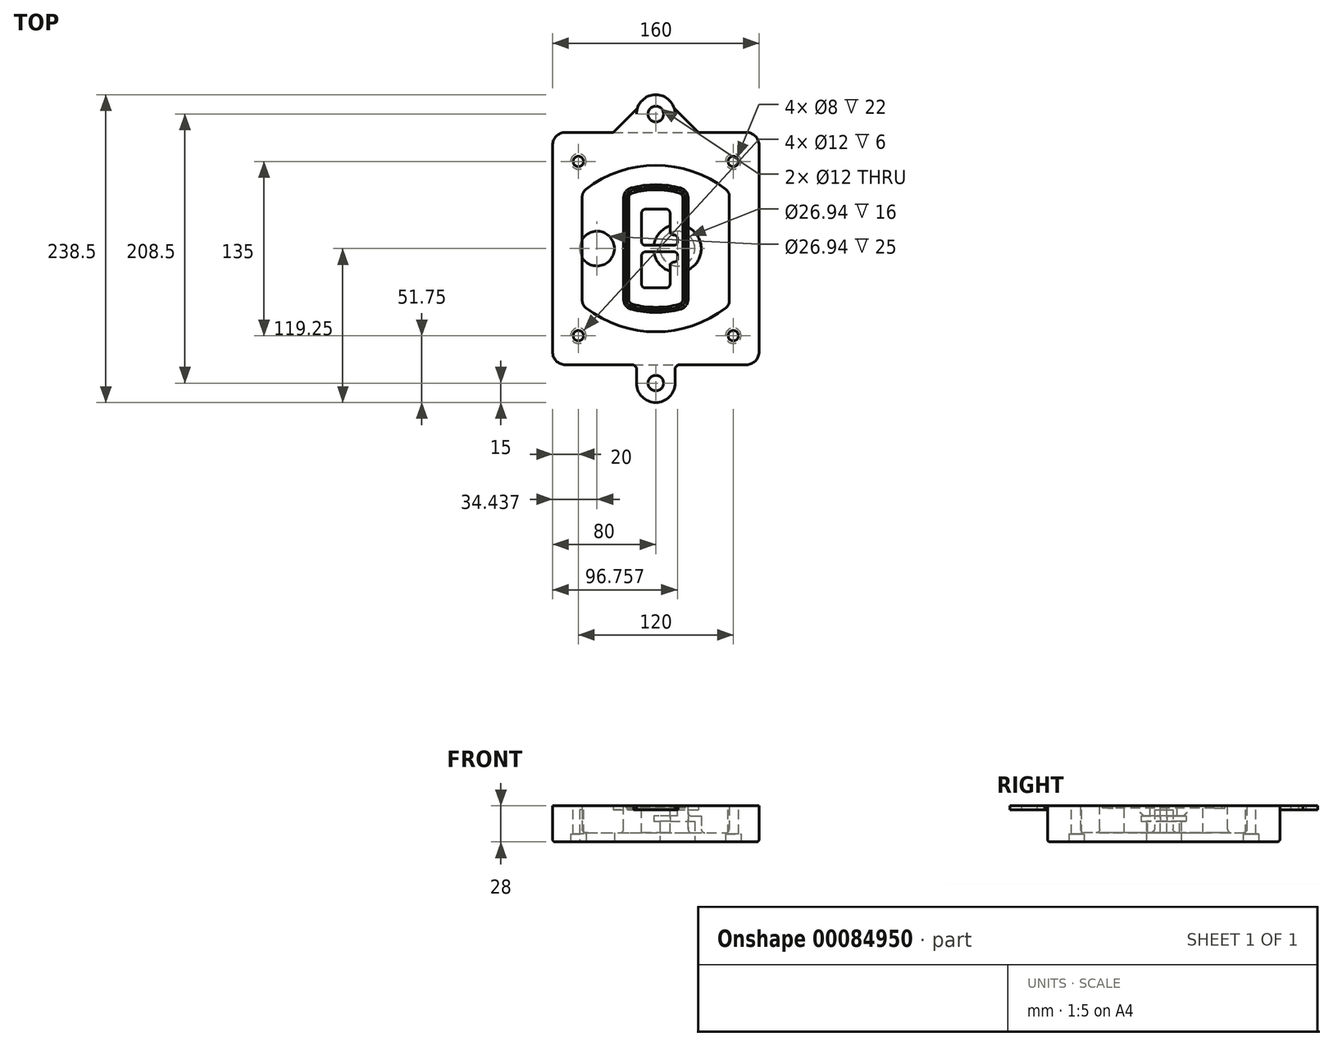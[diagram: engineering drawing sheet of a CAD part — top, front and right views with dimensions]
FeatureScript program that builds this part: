
annotation { "Feature Type Name" : "Feature", "Feature Type Description" : "" }
export const myFeature = defineFeature(function(context is Context, id is Id, definition is map)
    precondition{}
    {
        {
            var Q0;
            Q0=qCreatedBy(makeId("Top.planeOp"),FACE);
            var sketch = newSketch(context, id + "F0", { "sketchPlane" : qUnion([Q0])});
            skPoint(sketch, "E0.rect.middle", {"position": v(0, 0) * mm});
            skLineSegment(sketch, "E1.bottom", {"start": v(-70, -90) * mm, "end": v(70, -90) * mm});
            skLineSegment(sketch, "E1.top", {"start": v(-70, 90) * mm, "end": v(70, 90) * mm});
            skLineSegment(sketch, "E1.left", {"start": v(-80, -80) * mm, "end": v(-80, 80) * mm});
            skLineSegment(sketch, "E1.right", {"start": v(80, -80) * mm, "end": v(80, 80) * mm});
            skLineSegment(sketch, "E2", {"start": v(-80, 90) * mm, "end": v(80, -90) * mm, "construction": true});
            skLineSegment(sketch, "E3", {"start": v(80, 90) * mm, "end": v(-80, -90) * mm, "construction": true});
            skCircle(sketch, "E4", {"center": v(-60, 67.5) * mm, "radius": 4 * mm});
            skCircle(sketch, "E5", {"center": v(60, 67.5) * mm, "radius": 4 * mm});
            skCircle(sketch, "E6", {"center": v(60, -67.5) * mm, "radius": 4 * mm});
            skCircle(sketch, "E7", {"center": v(-60, -67.5) * mm, "radius": 4 * mm});
            skLineSegment(sketch, "E8", {"start": v(-60, 67.5) * mm, "end": v(60, 67.5) * mm, "construction": true});
            skLineSegment(sketch, "E9", {"start": v(60, 67.5) * mm, "end": v(60, -67.5) * mm, "construction": true});
            skLineSegment(sketch, "E10", {"start": v(60, -67.5) * mm, "end": v(-60, -67.5) * mm, "construction": true});
            skLineSegment(sketch, "E11", {"start": v(-60, -67.5) * mm, "end": v(-60, 67.5) * mm, "construction": true});
            skLineSegment(sketch, "E12", {"start": v(-60, 40.3) * mm, "end": v(-60, -40.3) * mm});
            skLineSegment(sketch, "E13", {"start": v(60, 40.3) * mm, "end": v(60, -40.3) * mm});
            skArc(sketch, "E14", {"start": v(56.15, 48.18) * mm, "mid": v(0, 67.5) * mm, "end": v(-56.15, 48.18) * mm});
            skArc(sketch, "E15", {"start": v(-56.15, -48.18) * mm, "mid": v(0, -67.5) * mm, "end": v(56.15, -48.18) * mm});
            skLineSegment(sketch, "E16", {"start": v(-60, 0) * mm, "end": v(60, 0) * mm, "construction": true});
            skPoint(sketch, "E17.visualSharp", {"position": v(-60, -45) * mm});
            skArc(sketch, "E17.filletArc", {"start": v(-60, -40.3) * mm, "mid": v(-58.99, -44.68) * mm, "end": v(-56.15, -48.18) * mm});
            skPoint(sketch, "E18.visualSharp", {"position": v(-60, 45) * mm});
            skArc(sketch, "E18.filletArc", {"start": v(-56.15, 48.18) * mm, "mid": v(-58.99, 44.68) * mm, "end": v(-60, 40.3) * mm});
            skPoint(sketch, "E19.visualSharp", {"position": v(60, 45) * mm});
            skArc(sketch, "E19.filletArc", {"start": v(60, 40.3) * mm, "mid": v(58.99, 44.68) * mm, "end": v(56.15, 48.18) * mm});
            skPoint(sketch, "E20.visualSharp", {"position": v(60, -45) * mm});
            skArc(sketch, "E20.filletArc", {"start": v(56.15, -48.18) * mm, "mid": v(58.99, -44.68) * mm, "end": v(60, -40.3) * mm});
            skPoint(sketch, "E21.visualSharp", {"position": v(-80, 90) * mm});
            skArc(sketch, "E21.filletArc", {"start": v(-70, 90) * mm, "mid": v(-77.07, 87.07) * mm, "end": v(-80, 80) * mm});
            skPoint(sketch, "E22.visualSharp", {"position": v(80, 90) * mm});
            skArc(sketch, "E22.filletArc", {"start": v(80, 80) * mm, "mid": v(77.07, 87.07) * mm, "end": v(70, 90) * mm});
            skPoint(sketch, "E23.visualSharp", {"position": v(80, -90) * mm});
            skArc(sketch, "E23.filletArc", {"start": v(70, -90) * mm, "mid": v(77.07, -87.07) * mm, "end": v(80, -80) * mm});
            skPoint(sketch, "E24.visualSharp", {"position": v(-80, -90) * mm});
            skArc(sketch, "E24.filletArc", {"start": v(-80, -80) * mm, "mid": v(-77.07, -87.07) * mm, "end": v(-70, -90) * mm});
            skArc(sketch, "E25.0", {"start": v(57, 40.3) * mm, "mid": v(56.3, 43.36) * mm, "end": v(54.3, 45.81) * mm});
            skLineSegment(sketch, "E25.1", {"start": v(57, 40.3) * mm, "end": v(57, -40.3) * mm});
            skArc(sketch, "E25.2", {"start": v(54.3, -45.81) * mm, "mid": v(56.3, -43.36) * mm, "end": v(57, -40.3) * mm});
            skArc(sketch, "E25.3", {"start": v(-54.3, -45.81) * mm, "mid": v(0, -64.5) * mm, "end": v(54.3, -45.81) * mm});
            skArc(sketch, "E25.4", {"start": v(-57, -40.3) * mm, "mid": v(-56.3, -43.36) * mm, "end": v(-54.3, -45.81) * mm});
            skArc(sketch, "E25.5", {"start": v(54.3, 45.81) * mm, "mid": v(0, 64.5) * mm, "end": v(-54.3, 45.81) * mm});
            skLineSegment(sketch, "E25.6", {"start": v(-57, 40.3) * mm, "end": v(-57, -40.3) * mm});
            skArc(sketch, "E25.7", {"start": v(-54.3, 45.81) * mm, "mid": v(-56.3, 43.36) * mm, "end": v(-57, 40.3) * mm});
            skArc(sketch, "E26.0", {"start": v(-58.62, 51.33) * mm, "mid": v(-62.58, 46.43) * mm, "end": v(-64, 40.3) * mm});
            skArc(sketch, "E26.1", {"start": v(58.62, 51.33) * mm, "mid": v(0, 71.5) * mm, "end": v(-58.62, 51.33) * mm});
            skArc(sketch, "E26.2", {"start": v(64, 40.3) * mm, "mid": v(62.58, 46.43) * mm, "end": v(58.62, 51.33) * mm});
            skLineSegment(sketch, "E26.3", {"start": v(64, 40.3) * mm, "end": v(64, -40.3) * mm});
            skArc(sketch, "E26.4", {"start": v(58.62, -51.33) * mm, "mid": v(62.58, -46.43) * mm, "end": v(64, -40.3) * mm});
            skLineSegment(sketch, "E26.5", {"start": v(-64, 40.3) * mm, "end": v(-64, -40.3) * mm});
            skArc(sketch, "E26.6", {"start": v(-58.62, -51.33) * mm, "mid": v(0, -71.5) * mm, "end": v(58.62, -51.33) * mm});
            skArc(sketch, "E26.7", {"start": v(-64, -40.3) * mm, "mid": v(-62.58, -46.43) * mm, "end": v(-58.62, -51.33) * mm});
            skSolve(sketch);
        }
        {
            var Q0;
            Q0=makeQuery(id+"F0.imprint","IMPRINT",FACE,{"disambiguationData":[TD([[makeQuery(id+"F0.imprint","IMPRINT",EDGE,{"derivedFrom":sQuery(id+"F0.wireOp",EDGE,"E1.bottom")}),1.0]])]});
            var Q1;
            Q1=makeQuery(id+"F0.imprint","IMPRINT",FACE,{"disambiguationData":[TD([[makeQuery(id+"F0.imprint","IMPRINT",EDGE,{"derivedFrom":sQuery(id+"F0.wireOp",EDGE,"E12")}),1.0]])]});
            var Q2;
            Q2=makeQuery(id+"F0.imprint","IMPRINT",FACE,{"disambiguationData":[TD([[makeQuery(id+"F0.imprint","IMPRINT",EDGE,{"derivedFrom":sQuery(id+"F0.wireOp",EDGE,"E25.0")}),1.0]])]});
            var Q3;
            Q3=makeQuery(id+"F0.imprint","IMPRINT",FACE,{"disambiguationData":[TD([[makeQuery(id+"F0.imprint","IMPRINT",EDGE,{"derivedFrom":sQuery(id+"F0.wireOp",EDGE,"E12")}),-1.0]])]});
            extrude(context, id + "F1", {"entities" : qUnion([Q0, Q1, Q2, Q3]), "oppositeDirection" : true, "depth" : 25 * mm});
        }
        {
            var Q0;
            Q0=makeQuery(id+"F0.imprint","IMPRINT",FACE,{"disambiguationData":[TD([[makeQuery(id+"F0.imprint","IMPRINT",EDGE,{"derivedFrom":sQuery(id+"F0.wireOp",EDGE,"E12")}),1.0]])]});
            extrude(context, id + "F2", {"entities" : qUnion([Q0]), "operationType" : NewBodyOperationType.ADD, "depth" : 3 * mm});
        }
        {
            var Q0;
            Q0=makeQuery(id+"F0.imprint","IMPRINT",FACE,{"disambiguationData":[TD([[makeQuery(id+"F0.imprint","IMPRINT",EDGE,{"derivedFrom":sQuery(id+"F0.wireOp",EDGE,"E25.0")}),1.0]])]});
            extrude(context, id + "F3", {"entities" : qUnion([Q0]), "operationType" : NewBodyOperationType.REMOVE, "oppositeDirection" : true, "depth" : 18 * mm});
        }
        {
            var Q0;
            Q0=makeQuery(id+"F2.opExtrude","CAP_FACE",FACE,{"disambiguationData":[OSD([sQuery(id+"F0.wireOp",EDGE,"E12"),sQuery(id+"F0.wireOp",EDGE,"E13"),sQuery(id+"F0.wireOp",EDGE,"E14"),sQuery(id+"F0.wireOp",EDGE,"E15"),sQuery(id+"F0.wireOp",EDGE,"E17.filletArc"),sQuery(id+"F0.wireOp",EDGE,"E18.filletArc"),sQuery(id+"F0.wireOp",EDGE,"E19.filletArc"),sQuery(id+"F0.wireOp",EDGE,"E20.filletArc"),sQuery(id+"F0.wireOp",EDGE,"E25.0"),sQuery(id+"F0.wireOp",EDGE,"E25.1"),sQuery(id+"F0.wireOp",EDGE,"E25.2"),sQuery(id+"F0.wireOp",EDGE,"E25.3"),sQuery(id+"F0.wireOp",EDGE,"E25.4"),sQuery(id+"F0.wireOp",EDGE,"E25.5"),sQuery(id+"F0.wireOp",EDGE,"E25.6"),sQuery(id+"F0.wireOp",EDGE,"E25.7")])],"isStart":false});
            var sketch = newSketch(context, id + "F4", { "sketchPlane" : qUnion([Q0])});
            skArc(sketch, "E27.0", {"start": v(-19.08, -46.97) * mm, "mid": v(0, -49.5) * mm, "end": v(19.08, -46.97) * mm});
            skArc(sketch, "E28.0", {"start": v(19.08, 46.97) * mm, "mid": v(0, 49.5) * mm, "end": v(-19.08, 46.97) * mm});
            skLineSegment(sketch, "E29", {"start": v(-25, 39.25) * mm, "end": v(-25, -39.25) * mm});
            skLineSegment(sketch, "E30", {"start": v(25, 39.25) * mm, "end": v(25, -39.25) * mm});
            skLineSegment(sketch, "E31", {"start": v(-25, 45.1) * mm, "end": v(25, 45.1) * mm, "construction": true});
            skLineSegment(sketch, "E32", {"start": v(-25, -45.1) * mm, "end": v(25, -45.1) * mm, "construction": true});
            skPoint(sketch, "E33.visualSharp", {"position": v(-25, 45.1) * mm});
            skArc(sketch, "E33.filletArc", {"start": v(-19.08, 46.97) * mm, "mid": v(-23.35, 44.11) * mm, "end": v(-25, 39.25) * mm});
            skPoint(sketch, "E34.visualSharp", {"position": v(25, 45.1) * mm});
            skArc(sketch, "E34.filletArc", {"start": v(25, 39.25) * mm, "mid": v(23.35, 44.11) * mm, "end": v(19.08, 46.97) * mm});
            skPoint(sketch, "E35.visualSharp", {"position": v(25, -45.1) * mm});
            skArc(sketch, "E35.filletArc", {"start": v(19.08, -46.97) * mm, "mid": v(23.35, -44.11) * mm, "end": v(25, -39.25) * mm});
            skPoint(sketch, "E36.visualSharp", {"position": v(-25, -45.1) * mm});
            skArc(sketch, "E36.filletArc", {"start": v(-25, -39.25) * mm, "mid": v(-23.35, -44.11) * mm, "end": v(-19.08, -46.97) * mm});
            skArc(sketch, "E37.0", {"start": v(54.3, 45.81) * mm, "mid": v(0, 64.5) * mm, "end": v(-54.3, 45.81) * mm});
            skArc(sketch, "E37.1", {"start": v(-54.3, 45.81) * mm, "mid": v(-56.3, 43.36) * mm, "end": v(-57, 40.3) * mm});
            skLineSegment(sketch, "E37.2", {"start": v(-57, 40.3) * mm, "end": v(-57, -40.3) * mm});
            skArc(sketch, "E37.3", {"start": v(-57, -40.3) * mm, "mid": v(-56.3, -43.36) * mm, "end": v(-54.3, -45.81) * mm});
            skArc(sketch, "E37.4", {"start": v(-54.3, -45.81) * mm, "mid": v(0, -64.5) * mm, "end": v(54.3, -45.81) * mm});
            skArc(sketch, "E37.5", {"start": v(54.3, -45.81) * mm, "mid": v(56.3, -43.36) * mm, "end": v(57, -40.3) * mm});
            skLineSegment(sketch, "E37.6", {"start": v(57, 40.3) * mm, "end": v(57, -40.3) * mm});
            skArc(sketch, "E37.7", {"start": v(57, 40.3) * mm, "mid": v(56.3, 43.36) * mm, "end": v(54.3, 45.81) * mm});
            skLineSegment(sketch, "E38.0", {"start": v(23, 39.25) * mm, "end": v(23, -39.25) * mm});
            skArc(sketch, "E38.1", {"start": v(18.56, -45.04) * mm, "mid": v(21.76, -42.9) * mm, "end": v(23, -39.25) * mm});
            skArc(sketch, "E38.2", {"start": v(-18.56, -45.04) * mm, "mid": v(0, -47.5) * mm, "end": v(18.56, -45.04) * mm});
            skArc(sketch, "E38.3", {"start": v(-23, -39.25) * mm, "mid": v(-21.76, -42.9) * mm, "end": v(-18.56, -45.04) * mm});
            skLineSegment(sketch, "E38.4", {"start": v(-23, 39.25) * mm, "end": v(-23, -39.25) * mm});
            skArc(sketch, "E38.5", {"start": v(23, 39.25) * mm, "mid": v(21.76, 42.9) * mm, "end": v(18.56, 45.04) * mm});
            skArc(sketch, "E38.6", {"start": v(-18.56, 45.04) * mm, "mid": v(-21.76, 42.9) * mm, "end": v(-23, 39.25) * mm});
            skArc(sketch, "E38.7", {"start": v(18.56, 45.04) * mm, "mid": v(0, 47.5) * mm, "end": v(-18.56, 45.04) * mm});
            skArc(sketch, "E39.0", {"start": v(21, 39.25) * mm, "mid": v(20.18, 41.68) * mm, "end": v(18.04, 43.1) * mm});
            skLineSegment(sketch, "E39.1", {"start": v(21, 39.25) * mm, "end": v(21, -39.25) * mm});
            skArc(sketch, "E39.2", {"start": v(18.04, -43.1) * mm, "mid": v(20.18, -41.68) * mm, "end": v(21, -39.25) * mm});
            skArc(sketch, "E39.3", {"start": v(-18.04, -43.1) * mm, "mid": v(0, -45.5) * mm, "end": v(18.04, -43.1) * mm});
            skArc(sketch, "E39.4", {"start": v(-21, -39.25) * mm, "mid": v(-20.18, -41.68) * mm, "end": v(-18.04, -43.1) * mm});
            skArc(sketch, "E39.5", {"start": v(18.04, 43.1) * mm, "mid": v(0, 45.5) * mm, "end": v(-18.04, 43.1) * mm});
            skLineSegment(sketch, "E39.6", {"start": v(-21, 39.25) * mm, "end": v(-21, -39.25) * mm});
            skArc(sketch, "E39.7", {"start": v(-18.04, 43.1) * mm, "mid": v(-20.18, 41.68) * mm, "end": v(-21, 39.25) * mm});
            skLineSegment(sketch, "E40", {"start": v(-25, 0) * mm, "end": v(25, 0) * mm, "construction": true});
            skLineSegment(sketch, "E41", {"start": v(-11, 5.5) * mm, "end": v(-11, 27.5) * mm});
            skLineSegment(sketch, "E42", {"start": v(-8, 30.5) * mm, "end": v(8, 30.5) * mm});
            skLineSegment(sketch, "E43", {"start": v(11, 27.5) * mm, "end": v(11, 13.5) * mm});
            skLineSegment(sketch, "E44", {"start": v(14, 10.5) * mm, "end": v(14, 10.5) * mm});
            skLineSegment(sketch, "E45", {"start": v(17, 7.5) * mm, "end": v(17, 5.5) * mm});
            skLineSegment(sketch, "E46", {"start": v(14, 2.5) * mm, "end": v(-8, 2.5) * mm});
            skPoint(sketch, "E47.visualSharp", {"position": v(-11, 30.5) * mm});
            skArc(sketch, "E47.filletArc", {"start": v(-8, 30.5) * mm, "mid": v(-10.12, 29.62) * mm, "end": v(-11, 27.5) * mm});
            skPoint(sketch, "E48.visualSharp", {"position": v(11, 30.5) * mm});
            skArc(sketch, "E48.filletArc", {"start": v(11, 27.5) * mm, "mid": v(10.12, 29.62) * mm, "end": v(8, 30.5) * mm});
            skPoint(sketch, "E49.visualSharp", {"position": v(11, 10.5) * mm});
            skArc(sketch, "E49.filletArc", {"start": v(11, 13.5) * mm, "mid": v(11.88, 11.38) * mm, "end": v(14, 10.5) * mm});
            skPoint(sketch, "E50.visualSharp", {"position": v(17, 10.5) * mm});
            skArc(sketch, "E50.filletArc", {"start": v(17, 7.5) * mm, "mid": v(16.12, 9.62) * mm, "end": v(14, 10.5) * mm});
            skPoint(sketch, "E51.visualSharp", {"position": v(17, 2.5) * mm});
            skArc(sketch, "E51.filletArc", {"start": v(14, 2.5) * mm, "mid": v(16.12, 3.38) * mm, "end": v(17, 5.5) * mm});
            skPoint(sketch, "E52.visualSharp", {"position": v(-11, 2.5) * mm});
            skArc(sketch, "E52.filletArc", {"start": v(-11, 5.5) * mm, "mid": v(-10.12, 3.38) * mm, "end": v(-8, 2.5) * mm});
            skLineSegment(sketch, "E53.0.MirrorCS", {"start": v(14, -2.5) * mm, "end": v(-8, -2.5) * mm});
            skArc(sketch, "E54.0.MirrorCS", {"start": v(-11, -5.5) * mm, "mid": v(-10.12, -3.38) * mm, "end": v(-8, -2.5) * mm});
            skLineSegment(sketch, "E55.0.MirrorCS", {"start": v(-11, -5.5) * mm, "end": v(-11, -27.5) * mm});
            skArc(sketch, "E56.0.MirrorCS", {"start": v(-8, -30.5) * mm, "mid": v(-10.12, -29.62) * mm, "end": v(-11, -27.5) * mm});
            skLineSegment(sketch, "E57.0.MirrorCS", {"start": v(-8, -30.5) * mm, "end": v(8, -30.5) * mm});
            skArc(sketch, "E58.0.MirrorCS", {"start": v(11, -27.5) * mm, "mid": v(10.12, -29.62) * mm, "end": v(8, -30.5) * mm});
            skLineSegment(sketch, "E59.0.MirrorCS", {"start": v(11, -27.5) * mm, "end": v(11, -13.5) * mm});
            skArc(sketch, "E60.0.MirrorCS", {"start": v(11, -13.5) * mm, "mid": v(11.88, -11.38) * mm, "end": v(14, -10.5) * mm});
            skArc(sketch, "E61.0.MirrorCS", {"start": v(17, -7.5) * mm, "mid": v(16.12, -9.62) * mm, "end": v(14, -10.5) * mm});
            skLineSegment(sketch, "E62.0.MirrorCS", {"start": v(17, -7.5) * mm, "end": v(17, -5.5) * mm});
            skArc(sketch, "E63.0.MirrorCS", {"start": v(14, -2.5) * mm, "mid": v(16.12, -3.38) * mm, "end": v(17, -5.5) * mm});
            skSolve(sketch);
        }
        {
            var Q0;
            Q0=makeQuery(id+"F4.imprint","IMPRINT",FACE,{"disambiguationData":[TD([[makeQuery(id+"F4.imprint","IMPRINT",EDGE,{"derivedFrom":sQuery(id+"F4.wireOp",EDGE,"E27.0")}),1.0]])]});
            var Q1;
            Q1=makeQuery(id+"F4.imprint","IMPRINT",FACE,{"disambiguationData":[TD([[makeQuery(id+"F4.imprint","IMPRINT",EDGE,{"derivedFrom":sQuery(id+"F4.wireOp",EDGE,"E38.0")}),-1.0]])]});
            var Q2;
            Q2=makeQuery(id+"F4.imprint","IMPRINT",FACE,{"disambiguationData":[TD([[makeQuery(id+"F4.imprint","IMPRINT",EDGE,{"derivedFrom":sQuery(id+"F4.wireOp",EDGE,"E39.0")}),1.0]])]});
            extrude(context, id + "F5", {"entities" : qUnion([Q0, Q1, Q2]), "operationType" : NewBodyOperationType.ADD, "endBound" : BoundingType.UP_TO_NEXT, "oppositeDirection" : true, "depth" : 25 * mm});
        }
        {
            var Q0;
            Q0=makeQuery(id+"F4.imprint","IMPRINT",FACE,{"disambiguationData":[TD([[makeQuery(id+"F4.imprint","IMPRINT",EDGE,{"derivedFrom":sQuery(id+"F4.wireOp",EDGE,"E38.0")}),-1.0]])]});
            extrude(context, id + "F6", {"entities" : qUnion([Q0]), "operationType" : NewBodyOperationType.REMOVE, "oppositeDirection" : true, "depth" : 2 * mm});
        }
        {
            var Q0;
            Q0=makeQuery(id+"F1.opExtrude","CAP_FACE",FACE,{"disambiguationData":[OSD([sQuery(id+"F0.wireOp",EDGE,"E1.bottom"),sQuery(id+"F0.wireOp",EDGE,"E1.top"),sQuery(id+"F0.wireOp",EDGE,"E1.left"),sQuery(id+"F0.wireOp",EDGE,"E1.right"),sQuery(id+"F0.wireOp",EDGE,"E4"),sQuery(id+"F0.wireOp",EDGE,"E5"),sQuery(id+"F0.wireOp",EDGE,"E6"),sQuery(id+"F0.wireOp",EDGE,"E7"),sQuery(id+"F0.wireOp",EDGE,"E21.filletArc"),sQuery(id+"F0.wireOp",EDGE,"E22.filletArc"),sQuery(id+"F0.wireOp",EDGE,"E23.filletArc"),sQuery(id+"F0.wireOp",EDGE,"E24.filletArc")])],"isStart":false});
            var sketch = newSketch(context, id + "F7", { "sketchPlane" : qUnion([Q0])});
            skCircle(sketch, "E64", {"center": v(16.76, 0) * mm, "radius": 13.47 * mm});
            skCircle(sketch, "E65", {"center": v(-45.56, 0) * mm, "radius": 13.47 * mm});
            skLineSegment(sketch, "E66", {"start": v(80, 0) * mm, "end": v(-80, 0) * mm});
            skCircle(sketch, "E67", {"center": v(16.76, 0) * mm, "radius": 18.47 * mm});
            skCircle(sketch, "E68", {"center": v(60, -67.5) * mm, "radius": 6 * mm});
            skCircle(sketch, "E69", {"center": v(-60, -67.5) * mm, "radius": 6 * mm});
            skCircle(sketch, "E70", {"center": v(-60, 67.5) * mm, "radius": 6 * mm});
            skCircle(sketch, "E71", {"center": v(60, 67.5) * mm, "radius": 6 * mm});
            skSolve(sketch);
        }
        {
            var Q0;
            {var subQ1=sQuery(id+"F7.wireOp",EDGE,"E66");var subQ4=sQuery(id+"F7.wireOp",EDGE,"E64");var subQ6=makeQuery(id+"F7.imprint","INTERSECT",VERTEX,{"disambiguationData":[OD(0.0)],"derivedFrom":[subQ4,subQ1]});Q0=makeQuery(id+"F7.imprint","IMPRINT",FACE,{"disambiguationData":[TD([[makeQuery(id+"F7.imprint","IMPRINT",EDGE,{"disambiguationData":[TD([[subQ6,-1.0]])],"derivedFrom":subQ4}),-1.0]])]});}
            var Q1;
            {var subQ0=sQuery(id+"F7.wireOp",EDGE,"E66");var subQ1=sQuery(id+"F7.wireOp",EDGE,"E64");var subQ3=makeQuery(id+"F7.imprint","INTERSECT",VERTEX,{"disambiguationData":[OD(0.0)],"derivedFrom":[subQ1,subQ0]});Q1=makeQuery(id+"F7.imprint","IMPRINT",FACE,{"disambiguationData":[TD([[makeQuery(id+"F7.imprint","IMPRINT",EDGE,{"disambiguationData":[TD([[subQ3,-1.0]])],"derivedFrom":subQ1}),1.0]])]});}
            var Q2;
            {var subQ0=sQuery(id+"F7.wireOp",EDGE,"E66");var subQ1=sQuery(id+"F7.wireOp",EDGE,"E64");var subQ3=makeQuery(id+"F7.imprint","INTERSECT",VERTEX,{"disambiguationData":[OD(0.0)],"derivedFrom":[subQ1,subQ0]});Q2=makeQuery(id+"F7.imprint","IMPRINT",FACE,{"disambiguationData":[TD([[makeQuery(id+"F7.imprint","IMPRINT",EDGE,{"disambiguationData":[TD([[subQ3,1.0]])],"derivedFrom":subQ1}),1.0]])]});}
            var Q3;
            {var subQ1=sQuery(id+"F7.wireOp",EDGE,"E66");var subQ4=sQuery(id+"F7.wireOp",EDGE,"E64");var subQ6=makeQuery(id+"F7.imprint","INTERSECT",VERTEX,{"disambiguationData":[OD(0.0)],"derivedFrom":[subQ4,subQ1]});Q3=makeQuery(id+"F7.imprint","IMPRINT",FACE,{"disambiguationData":[TD([[makeQuery(id+"F7.imprint","IMPRINT",EDGE,{"disambiguationData":[TD([[subQ6,1.0]])],"derivedFrom":subQ4}),-1.0]])]});}
            extrude(context, id + "F8", {"entities" : qUnion([Q0, Q1, Q2, Q3]), "operationType" : NewBodyOperationType.ADD, "oppositeDirection" : true, "depth" : 20 * mm});
        }
        {
            var Q0;
            {var subQ0=sQuery(id+"F7.wireOp",EDGE,"E66");var subQ1=sQuery(id+"F7.wireOp",EDGE,"E64");var subQ3=makeQuery(id+"F7.imprint","INTERSECT",VERTEX,{"disambiguationData":[OD(0.0)],"derivedFrom":[subQ1,subQ0]});Q0=makeQuery(id+"F7.imprint","IMPRINT",FACE,{"disambiguationData":[TD([[makeQuery(id+"F7.imprint","IMPRINT",EDGE,{"disambiguationData":[TD([[subQ3,-1.0]])],"derivedFrom":subQ1}),1.0]])]});}
            var Q1;
            {var subQ0=sQuery(id+"F7.wireOp",EDGE,"E66");var subQ1=sQuery(id+"F7.wireOp",EDGE,"E64");var subQ3=makeQuery(id+"F7.imprint","INTERSECT",VERTEX,{"disambiguationData":[OD(0.0)],"derivedFrom":[subQ1,subQ0]});Q1=makeQuery(id+"F7.imprint","IMPRINT",FACE,{"disambiguationData":[TD([[makeQuery(id+"F7.imprint","IMPRINT",EDGE,{"disambiguationData":[TD([[subQ3,1.0]])],"derivedFrom":subQ1}),1.0]])]});}
            extrude(context, id + "F9", {"entities" : qUnion([Q0, Q1]), "operationType" : NewBodyOperationType.REMOVE, "oppositeDirection" : true, "depth" : 16 * mm});
        }
        {
            var Q0;
            {var subQ0=sQuery(id+"F7.wireOp",EDGE,"E66");var subQ1=sQuery(id+"F7.wireOp",EDGE,"E65");var subQ3=makeQuery(id+"F7.imprint","INTERSECT",VERTEX,{"disambiguationData":[OD(0.0)],"derivedFrom":[subQ1,subQ0]});Q0=makeQuery(id+"F7.imprint","IMPRINT",FACE,{"disambiguationData":[TD([[makeQuery(id+"F7.imprint","IMPRINT",EDGE,{"disambiguationData":[TD([[subQ3,-1.0]])],"derivedFrom":subQ1}),1.0]])]});}
            var Q1;
            {var subQ0=sQuery(id+"F7.wireOp",EDGE,"E66");var subQ1=sQuery(id+"F7.wireOp",EDGE,"E65");var subQ3=makeQuery(id+"F7.imprint","INTERSECT",VERTEX,{"disambiguationData":[OD(0.0)],"derivedFrom":[subQ1,subQ0]});Q1=makeQuery(id+"F7.imprint","IMPRINT",FACE,{"disambiguationData":[TD([[makeQuery(id+"F7.imprint","IMPRINT",EDGE,{"disambiguationData":[TD([[subQ3,1.0]])],"derivedFrom":subQ1}),1.0]])]});}
            extrude(context, id + "F10", {"entities" : qUnion([Q0, Q1]), "operationType" : NewBodyOperationType.REMOVE, "oppositeDirection" : true, "depth" : 25 * mm});
        }
        {
            var Q0;
            Q0=makeQuery(id+"F7.imprint","IMPRINT",FACE,{"disambiguationData":[TD([[makeQuery(id+"F7.imprint","IMPRINT",EDGE,{"derivedFrom":sQuery(id+"F7.wireOp",EDGE,"E68")}),1.0]])]});
            var Q1;
            Q1=makeQuery(id+"F7.imprint","IMPRINT",FACE,{"disambiguationData":[TD([[makeQuery(id+"F7.imprint","IMPRINT",EDGE,{"derivedFrom":makeQuery(id+"F1.opExtrude","CAP_EDGE",EDGE,{"disambiguationData":[OSD([sQuery(id+"F0.wireOp",EDGE,"E5")])],"isStart":false})}),-1.0]])]});
            var Q2;
            Q2=makeQuery(id+"F7.imprint","IMPRINT",FACE,{"disambiguationData":[TD([[makeQuery(id+"F7.imprint","IMPRINT",EDGE,{"derivedFrom":sQuery(id+"F7.wireOp",EDGE,"E69")}),1.0]])]});
            var Q3;
            Q3=makeQuery(id+"F7.imprint","IMPRINT",FACE,{"disambiguationData":[TD([[makeQuery(id+"F7.imprint","IMPRINT",EDGE,{"derivedFrom":makeQuery(id+"F1.opExtrude","CAP_EDGE",EDGE,{"disambiguationData":[OSD([sQuery(id+"F0.wireOp",EDGE,"E4")])],"isStart":false})}),-1.0]])]});
            var Q4;
            Q4=makeQuery(id+"F7.imprint","IMPRINT",FACE,{"disambiguationData":[TD([[makeQuery(id+"F7.imprint","IMPRINT",EDGE,{"derivedFrom":sQuery(id+"F7.wireOp",EDGE,"E70")}),1.0]])]});
            var Q5;
            Q5=makeQuery(id+"F7.imprint","IMPRINT",FACE,{"disambiguationData":[TD([[makeQuery(id+"F7.imprint","IMPRINT",EDGE,{"derivedFrom":makeQuery(id+"F1.opExtrude","CAP_EDGE",EDGE,{"disambiguationData":[OSD([sQuery(id+"F0.wireOp",EDGE,"E7")])],"isStart":false})}),-1.0]])]});
            var Q6;
            Q6=makeQuery(id+"F7.imprint","IMPRINT",FACE,{"disambiguationData":[TD([[makeQuery(id+"F7.imprint","IMPRINT",EDGE,{"derivedFrom":sQuery(id+"F7.wireOp",EDGE,"E71")}),1.0]])]});
            var Q7;
            Q7=makeQuery(id+"F7.imprint","IMPRINT",FACE,{"disambiguationData":[TD([[makeQuery(id+"F7.imprint","IMPRINT",EDGE,{"derivedFrom":makeQuery(id+"F1.opExtrude","CAP_EDGE",EDGE,{"disambiguationData":[OSD([sQuery(id+"F0.wireOp",EDGE,"E6")])],"isStart":false})}),-1.0]])]});
            extrude(context, id + "F11", {"entities" : qUnion([Q0, Q1, Q2, Q3, Q4, Q5, Q6, Q7]), "operationType" : NewBodyOperationType.REMOVE, "oppositeDirection" : true, "depth" : 6 * mm});
        }
        {
            var Q0;
            Q0=makeQuery(id+"F9.boolean.opBoolean","COPY",FACE,{"derivedFrom":makeQuery(id+"F9.opExtrude","CAP_FACE",FACE,{"disambiguationData":[OSD([sQuery(id+"F7.wireOp",EDGE,"E64")])],"isStart":false})});
            var sketch = newSketch(context, id + "F12", { "sketchPlane" : qUnion([Q0])});
            skArc(sketch, "E72.0", {"start": v(11, 17.55) * mm, "mid": v(2.57, 11.82) * mm, "end": v(-1.54, 2.5) * mm});
            skArc(sketch, "E72.1", {"start": v(-1.54, -2.5) * mm, "mid": v(2.57, -11.82) * mm, "end": v(11, -17.55) * mm});
            skLineSegment(sketch, "E73", {"start": v(-1.54, -2.5) * mm, "end": v(14, -2.5) * mm});
            skLineSegment(sketch, "E74.0", {"start": v(14, 2.5) * mm, "end": v(-1.54, 2.5) * mm});
            skArc(sketch, "E74.1", {"start": v(14, 2.5) * mm, "mid": v(16.12, 3.38) * mm, "end": v(17, 5.5) * mm});
            skLineSegment(sketch, "E74.2", {"start": v(17, 7.5) * mm, "end": v(17, 5.5) * mm});
            skArc(sketch, "E74.3", {"start": v(17, 7.5) * mm, "mid": v(16.12, 9.62) * mm, "end": v(14, 10.5) * mm});
            skArc(sketch, "E74.4", {"start": v(11, 13.5) * mm, "mid": v(11.88, 11.38) * mm, "end": v(14, 10.5) * mm});
            skLineSegment(sketch, "E74.5", {"start": v(11, 17.55) * mm, "end": v(11, 13.5) * mm});
            skLineSegment(sketch, "E74.7", {"start": v(14, -2.5) * mm, "end": v(-1.54, -2.5) * mm});
            skArc(sketch, "E74.8", {"start": v(14, -2.5) * mm, "mid": v(16.12, -3.38) * mm, "end": v(17, -5.5) * mm});
            skLineSegment(sketch, "E74.9", {"start": v(17, -7.5) * mm, "end": v(17, -5.5) * mm});
            skArc(sketch, "E74.10", {"start": v(17, -7.5) * mm, "mid": v(16.12, -9.62) * mm, "end": v(14, -10.5) * mm});
            skArc(sketch, "E74.11", {"start": v(11, -13.5) * mm, "mid": v(11.88, -11.38) * mm, "end": v(14, -10.5) * mm});
            skLineSegment(sketch, "E74.12", {"start": v(11, -17.55) * mm, "end": v(11, -13.5) * mm});
            skPoint(sketch, "E75.orphan", {"position": v(11, -27.5) * mm});
            skPoint(sketch, "E76.orphan", {"position": v(-8, -2.5) * mm});
            skPoint(sketch, "E77.orphan", {"position": v(-8, 2.5) * mm});
            skPoint(sketch, "E78.orphan", {"position": v(11, 27.5) * mm});
            skSolve(sketch);
        }
        {
            var Q0;
            {var subQ7=sQuery(id+"F12.wireOp",EDGE,"E72.0");var subQ14=sQuery(id+"F12.wireOp",EDGE,"E72.1");var subQ16=sQuery(id+"F12.wireOp",EDGE,"E74.1");var subQ18=sQuery(id+"F12.wireOp",EDGE,"E74.8");Q0=qUnion([makeQuery(id+"F12.imprint","IMPRINT",FACE,{"disambiguationData":[TD([[makeQuery(id+"F12.imprint","IMPRINT",EDGE,{"derivedFrom":subQ7}),1.0]])]}),makeQuery(id+"F12.imprint","IMPRINT",FACE,{"disambiguationData":[TD([[makeQuery(id+"F12.imprint","IMPRINT",EDGE,{"derivedFrom":subQ14}),1.0]])]}),makeQuery(id+"F12.imprint","IMPRINT",FACE,{"disambiguationData":[TD([[makeQuery(id+"F12.imprint","IMPRINT",EDGE,{"derivedFrom":subQ16}),1.0]])]}),makeQuery(id+"F12.imprint","IMPRINT",FACE,{"disambiguationData":[TD([[makeQuery(id+"F12.imprint","IMPRINT",EDGE,{"derivedFrom":subQ18}),-1.0]])]})]);}
            var Q1;
            Q1=makeQuery(id+"F5.boolean.opBoolean","SPLIT",FACE,{"disambiguationData":[TD([makeQuery(id+"F5.opExtrude","SWEPT_FACE",FACE,{"disambiguationData":[OSD([sQuery(id+"F4.wireOp",EDGE,"E41")])]})])],"derivedFrom":makeQuery(id+"F3.boolean.opBoolean","COPY",FACE,{"derivedFrom":makeQuery(id+"F3.opExtrude","CAP_FACE",FACE,{"disambiguationData":[OSD([sQuery(id+"F0.wireOp",EDGE,"E25.0"),sQuery(id+"F0.wireOp",EDGE,"E25.1"),sQuery(id+"F0.wireOp",EDGE,"E25.2"),sQuery(id+"F0.wireOp",EDGE,"E25.3"),sQuery(id+"F0.wireOp",EDGE,"E25.4"),sQuery(id+"F0.wireOp",EDGE,"E25.5"),sQuery(id+"F0.wireOp",EDGE,"E25.6"),sQuery(id+"F0.wireOp",EDGE,"E25.7")])],"isStart":false})})});
            extrude(context, id + "F13", {"entities" : qUnion([Q0]), "operationType" : NewBodyOperationType.REMOVE, "endBound" : BoundingType.UP_TO_SURFACE, "endBoundEntityFace" : qUnion([Q1]), "depth" : 25 * mm});
        }
        {
            var Q0;
            Q0=makeQuery(id+"F3.boolean.opBoolean","COPY",EDGE,{"derivedFrom":makeQuery(id+"F3.opExtrude","CAP_EDGE",EDGE,{"disambiguationData":[OSD([sQuery(id+"F0.wireOp",EDGE,"E25.6")])],"isStart":false})});
            var Q1;
            Q1=makeQuery(id+"F8.boolean.opBoolean","INTERSECT",EDGE,{"derivedFrom":[makeQuery(id+"F5.opExtrude","SWEPT_FACE",FACE,{"disambiguationData":[OSD([sQuery(id+"F4.wireOp",EDGE,"E30")])]}),makeQuery(id+"F8.opExtrude","CAP_FACE",FACE,{"disambiguationData":[OSD([sQuery(id+"F7.wireOp",EDGE,"E67")])],"isStart":false})]});
            var Q2;
            Q2=makeQuery(id+"F8.boolean.opBoolean","INTERSECT",EDGE,{"disambiguationData":[OD(1.0)],"derivedFrom":[makeQuery(id+"F5.opExtrude","SWEPT_FACE",FACE,{"disambiguationData":[OSD([sQuery(id+"F4.wireOp",EDGE,"E30")])]}),makeQuery(id+"F8.opExtrude","SWEPT_FACE",FACE,{"disambiguationData":[OSD([sQuery(id+"F7.wireOp",EDGE,"E67")])]})]});
            var Q3;
            {var subQ0=sQuery(id+"F4.wireOp",EDGE,"E30");Q3=makeQuery(id+"F8.boolean.opBoolean","SPLIT",EDGE,{"disambiguationData":[TD([makeQuery(id+"F5.opExtrude","SWEPT_FACE",FACE,{"disambiguationData":[OSD([sQuery(id+"F4.wireOp",EDGE,"E35.filletArc")])]})])],"derivedFrom":makeQuery(id+"F5.opExtrude","CAP_EDGE",EDGE,{"disambiguationData":[OSD([subQ0])],"isStart":false})});}
            var Q4;
            {var subQ0=sQuery(id+"F0.wireOp",EDGE,"E25.7");var subQ1=sQuery(id+"F0.wireOp",EDGE,"E25.1");var subQ2=sQuery(id+"F0.wireOp",EDGE,"E25.6");var subQ3=sQuery(id+"F0.wireOp",EDGE,"E25.5");var subQ4=sQuery(id+"F0.wireOp",EDGE,"E25.4");var subQ5=sQuery(id+"F0.wireOp",EDGE,"E25.0");var subQ6=sQuery(id+"F0.wireOp",EDGE,"E25.2");var subQ7=sQuery(id+"F0.wireOp",EDGE,"E25.3");Q4=makeQuery(id+"F8.boolean.opBoolean","INTERSECT",EDGE,{"derivedFrom":[makeQuery(id+"F5.boolean.opBoolean","SPLIT",FACE,{"disambiguationData":[TD([makeQuery(id+"F2.opExtrude","SWEPT_FACE",FACE,{"disambiguationData":[OSD([subQ5])]})])],"derivedFrom":makeQuery(id+"F3.boolean.opBoolean","COPY",FACE,{"derivedFrom":makeQuery(id+"F3.opExtrude","CAP_FACE",FACE,{"disambiguationData":[OSD([subQ5,subQ1,subQ6,subQ7,subQ4,subQ3,subQ2,subQ0])],"isStart":false})})}),makeQuery(id+"F8.opExtrude","SWEPT_FACE",FACE,{"disambiguationData":[OSD([sQuery(id+"F7.wireOp",EDGE,"E67")])]})]});}
            var Q5;
            Q5=makeQuery(id+"F8.boolean.opBoolean","INTERSECT",EDGE,{"disambiguationData":[OD(0.0)],"derivedFrom":[makeQuery(id+"F5.opExtrude","SWEPT_FACE",FACE,{"disambiguationData":[OSD([sQuery(id+"F4.wireOp",EDGE,"E30")])]}),makeQuery(id+"F8.opExtrude","SWEPT_FACE",FACE,{"disambiguationData":[OSD([sQuery(id+"F7.wireOp",EDGE,"E67")])]})]});
            fillet(context, id + "F14", {"entities" : qUnion([Q0, Q1, Q2, Q3, Q4, Q5]), "radius" : 3 * mm, "tangentPropagation" : true, "allowEdgeOverflow" : false});
        }
        {
            var Q0;
            Q0=makeQuery(id+"F1.opExtrude","CAP_EDGE",EDGE,{"disambiguationData":[OSD([sQuery(id+"F0.wireOp",EDGE,"E1.bottom")])],"isStart":false});
            fillet(context, id + "F15", {"entities" : qUnion([Q0]), "radius" : 2 * mm, "tangentPropagation" : true, "allowEdgeOverflow" : false});
        }
        {
            var Q0;
            {var subQ0=sQuery(id+"F0.wireOp",EDGE,"E22.filletArc");var subQ1=sQuery(id+"F0.wireOp",EDGE,"E7");var subQ2=sQuery(id+"F0.wireOp",EDGE,"E6");var subQ3=sQuery(id+"F0.wireOp",EDGE,"E5");var subQ4=sQuery(id+"F0.wireOp",EDGE,"E4");var subQ5=sQuery(id+"F0.wireOp",EDGE,"E1.bottom");var subQ6=sQuery(id+"F0.wireOp",EDGE,"E21.filletArc");var subQ7=sQuery(id+"F0.wireOp",EDGE,"E1.top");var subQ8=sQuery(id+"F0.wireOp",EDGE,"E1.left");var subQ9=sQuery(id+"F0.wireOp",EDGE,"E1.right");var subQ10=sQuery(id+"F0.wireOp",EDGE,"E23.filletArc");var subQ11=sQuery(id+"F0.wireOp",EDGE,"E24.filletArc");Q0=makeQuery(id+"F2.boolean.opBoolean","SPLIT",FACE,{"disambiguationData":[TD([makeQuery(id+"F1.opExtrude","SWEPT_FACE",FACE,{"disambiguationData":[OSD([subQ5])]})])],"derivedFrom":makeQuery(id+"F1.opExtrude","CAP_FACE",FACE,{"disambiguationData":[OSD([subQ5,subQ7,subQ8,subQ9,subQ4,subQ3,subQ2,subQ1,subQ6,subQ0,subQ10,subQ11])],"isStart":true})});}
            var sketch = newSketch(context, id + "F16", { "sketchPlane" : qUnion([Q0])});
            skCircle(sketch, "E79", {"center": v(0, 104.25) * mm, "radius": 6 * mm});
            skArc(sketch, "E80", {"start": v(15, 104.25) * mm, "mid": v(0, 119.25) * mm, "end": v(-15, 104.25) * mm});
            skLineSegment(sketch, "E81", {"start": v(-15, 108) * mm, "end": v(-15, 104.25) * mm});
            skLineSegment(sketch, "E82", {"start": v(15, 108) * mm, "end": v(15, 104.25) * mm});
            skLineSegment(sketch, "E83", {"start": v(-15, 108) * mm, "end": v(-33, 90) * mm});
            skLineSegment(sketch, "E84", {"start": v(15, 108) * mm, "end": v(33, 90) * mm});
            skLineSegment(sketch, "E85.MirrorCS", {"start": v(-15, -92.25) * mm, "end": v(-33, -74.25) * mm});
            skLineSegment(sketch, "E86.MirrorCS", {"start": v(15, -92.25) * mm, "end": v(33, -74.25) * mm});
            skLineSegment(sketch, "E87.MirrorCS", {"start": v(15, -104.25) * mm, "end": v(15, -92.25) * mm});
            skLineSegment(sketch, "E88.MirrorCS", {"start": v(-15, -104.25) * mm, "end": v(-15, -92.25) * mm});
            skArc(sketch, "E89.MirrorCS", {"start": v(15, -104.25) * mm, "mid": v(0, -119.25) * mm, "end": v(-15, -104.25) * mm});
            skCircle(sketch, "E90.MirrorC", {"center": v(0, -104.25) * mm, "radius": 6 * mm});
            skSolve(sketch);
        }
        {
            var Q0;
            Q0=makeQuery(id+"F16.imprint","IMPRINT",FACE,{"disambiguationData":[TD([[makeQuery(id+"F16.imprint","IMPRINT",EDGE,{"derivedFrom":sQuery(id+"F16.wireOp",EDGE,"E79")}),-1.0]])]});
            var Q1;
            Q1=makeQuery(id+"F16.imprint","IMPRINT",FACE,{"disambiguationData":[TD([[makeQuery(id+"F16.imprint","IMPRINT",EDGE,{"derivedFrom":makeQuery(id+"F1.opExtrude","CAP_EDGE",EDGE,{"disambiguationData":[OSD([sQuery(id+"F0.wireOp",EDGE,"E1.left")])],"isStart":true})}),-1.0]])]});
            var Q2;
            {var subQ0=sQuery(id+"F16.wireOp",EDGE,"E85.MirrorCS");Q2=makeQuery(id+"F16.imprint","IMPRINT",FACE,{"disambiguationData":[TD([[makeQuery(id+"F16.imprint","IMPRINT",EDGE,{"derivedFrom":subQ0}),-1.0]])]});}
            var Q3;
            Q3=makeQuery(id+"F2.opExtrude","CAP_FACE",FACE,{"disambiguationData":[OSD([sQuery(id+"F0.wireOp",EDGE,"E12"),sQuery(id+"F0.wireOp",EDGE,"E13"),sQuery(id+"F0.wireOp",EDGE,"E14"),sQuery(id+"F0.wireOp",EDGE,"E15"),sQuery(id+"F0.wireOp",EDGE,"E17.filletArc"),sQuery(id+"F0.wireOp",EDGE,"E18.filletArc"),sQuery(id+"F0.wireOp",EDGE,"E19.filletArc"),sQuery(id+"F0.wireOp",EDGE,"E20.filletArc"),sQuery(id+"F0.wireOp",EDGE,"E25.0"),sQuery(id+"F0.wireOp",EDGE,"E25.1"),sQuery(id+"F0.wireOp",EDGE,"E25.2"),sQuery(id+"F0.wireOp",EDGE,"E25.3"),sQuery(id+"F0.wireOp",EDGE,"E25.4"),sQuery(id+"F0.wireOp",EDGE,"E25.5"),sQuery(id+"F0.wireOp",EDGE,"E25.6"),sQuery(id+"F0.wireOp",EDGE,"E25.7")])],"isStart":false});
            extrude(context, id + "F17", {"entities" : qUnion([Q0, Q1, Q2]), "operationType" : NewBodyOperationType.ADD, "endBound" : BoundingType.UP_TO_SURFACE, "endBoundEntityFace" : qUnion([Q3]), "depth" : 25 * mm});
        }
    });
